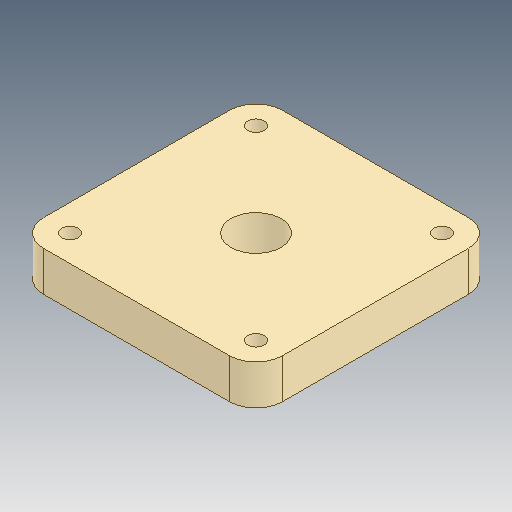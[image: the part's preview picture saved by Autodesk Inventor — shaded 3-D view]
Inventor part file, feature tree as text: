
AUTODESK INVENTOR PART (.ipt)
format: ipt  version: 2020 (Build 240168000, 168)  size: 122,880 bytes
history: native  units: mm
features: mirror x2, other x1, extrude x1, sketch x1
ambient origin geometry x8: Origin, YZ Plane, XZ Plane, XY Plane, X Axis, Y Axis, Z Axis, Center Point
bodies: Body1 (feature_tree)
feature tree (5):
  other  "Sólido1"
  extrude  "Extrusão1"  Depth=36.0mm
  mirror  "Espelhamento1"
  mirror  "Espelhamento2"
  sketch  "Esboço1"  dims[d0=15.1mm d1=36.0mm d2=36.0mm d3=8.0mm d4=5.0mm d5=12.0mm d6=0.0mm d7=8.0mm d8=8.0mm]
